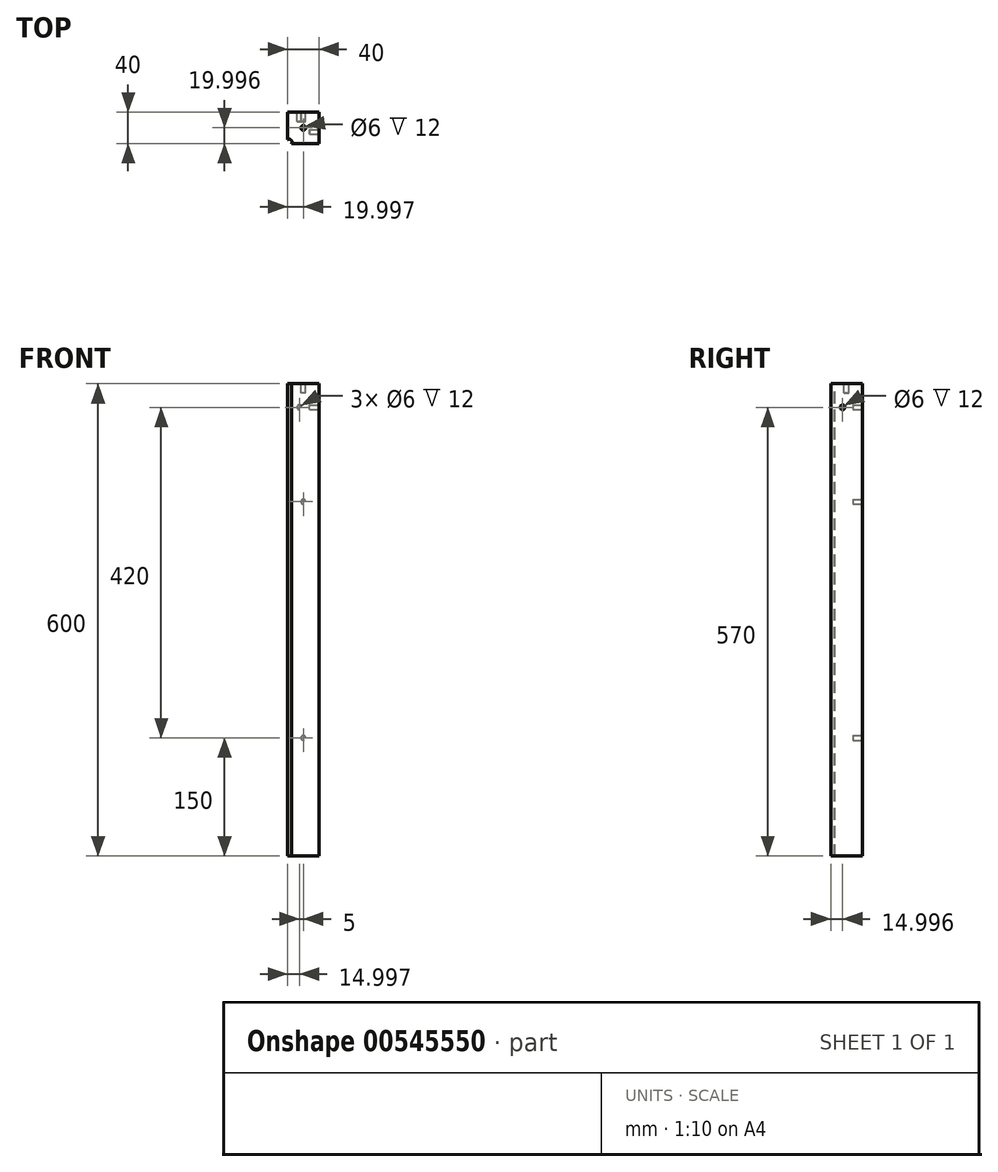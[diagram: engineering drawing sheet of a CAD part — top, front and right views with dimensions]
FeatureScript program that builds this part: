
annotation { "Feature Type Name" : "Feature", "Feature Type Description" : "" }
export const myFeature = defineFeature(function(context is Context, id is Id, definition is map)
    precondition{}
    {
        {
            var Q0;
            Q0=qCreatedBy(makeId("Top.planeOp"),FACE);
            var sketch = newSketch(context, id + "F0", { "sketchPlane" : qUnion([Q0])});
            skLineSegment(sketch, "E0.bottom", {"start": v(-52.47, 52.39) * mm, "end": v(-12.47, 52.39) * mm});
            skLineSegment(sketch, "E0.top", {"start": v(-52.47, 12.39) * mm, "end": v(-12.47, 12.39) * mm});
            skLineSegment(sketch, "E0.left", {"start": v(-52.47, 52.39) * mm, "end": v(-52.47, 12.39) * mm});
            skLineSegment(sketch, "E0.right", {"start": v(-12.47, 52.39) * mm, "end": v(-12.47, 12.39) * mm});
            skSolve(sketch);
        }
        {
            var Q0;
            Q0=makeQuery(id+"F0.imprint","IMPRINT",FACE,{"disambiguationData":[TD([[makeQuery(id+"F0.imprint","IMPRINT",EDGE,{"derivedFrom":sQuery(id+"F0.wireOp",EDGE,"E0.bottom")}),-1.0]])]});
            extrude(context, id + "F1", {"entities" : qUnion([Q0]), "depth" : 600 * mm, "offsetDistance" : 25 * mm});
        }
        {
            var Q0;
            Q0=makeQuery(id+"F1.opExtrude","SWEPT_FACE",FACE,{"disambiguationData":[OSD([sQuery(id+"F0.wireOp",EDGE,"E0.right")])]});
            var sketch = newSketch(context, id + "F2", { "sketchPlane" : qUnion([Q0])});
            skCircle(sketch, "E1", {"center": v(27.39, 570) * mm, "radius": 3 * mm});
            skSolve(sketch);
        }
        {
            var Q0;
            Q0=makeQuery(id+"F2.imprint","IMPRINT",FACE,{"disambiguationData":[TD([[makeQuery(id+"F2.imprint","IMPRINT",EDGE,{"derivedFrom":sQuery(id+"F2.wireOp",EDGE,"E1")}),1.0]])]});
            extrude(context, id + "F3", {"entities" : qUnion([Q0]), "operationType" : NewBodyOperationType.REMOVE, "oppositeDirection" : true, "depth" : 12 * mm, "offsetDistance" : 25 * mm});
        }
        {
            var Q0;
            Q0=makeQuery(id+"F1.opExtrude","SWEPT_FACE",FACE,{"disambiguationData":[OSD([sQuery(id+"F0.wireOp",EDGE,"E0.bottom")])]});
            var sketch = newSketch(context, id + "F4", { "sketchPlane" : qUnion([Q0])});
            skCircle(sketch, "E2", {"center": v(37.47, 570) * mm, "radius": 3 * mm});
            skCircle(sketch, "E3", {"center": v(32.47, 450) * mm, "radius": 3 * mm});
            skSolve(sketch);
        }
        {
            var Q0;
            Q0=makeQuery(id+"F4.imprint","IMPRINT",FACE,{"disambiguationData":[TD([[makeQuery(id+"F4.imprint","IMPRINT",EDGE,{"derivedFrom":sQuery(id+"F4.wireOp",EDGE,"E2")}),1.0]])]});
            extrude(context, id + "F5", {"entities" : qUnion([Q0]), "operationType" : NewBodyOperationType.REMOVE, "oppositeDirection" : true, "depth" : 12 * mm, "offsetDistance" : 25 * mm});
        }
        {
            var Q0;
            Q0=makeQuery(id+"F1.opExtrude","CAP_FACE",FACE,{"disambiguationData":[OSD([sQuery(id+"F0.wireOp",EDGE,"E0.bottom"),sQuery(id+"F0.wireOp",EDGE,"E0.top"),sQuery(id+"F0.wireOp",EDGE,"E0.left"),sQuery(id+"F0.wireOp",EDGE,"E0.right")])],"isStart":false});
            var sketch = newSketch(context, id + "F6", { "sketchPlane" : qUnion([Q0])});
            skCircle(sketch, "E4", {"center": v(-50.47, 14.39) * mm, "radius": 3.54 * mm});
            skSolve(sketch);
        }
        {
            var Q0;
            {var subQ0=sQuery(id+"F6.wireOp",EDGE,"E4");var subQ1=makeQuery(id+"F1.opExtrude","CAP_EDGE",EDGE,{"disambiguationData":[OSD([sQuery(id+"F0.wireOp",EDGE,"E0.top")])],"isStart":false});var subQ2=makeQuery(id+"F6.imprint","INTERSECT",VERTEX,{"derivedFrom":[subQ1,subQ0]});Q0=makeQuery(id+"F6.imprint","IMPRINT",FACE,{"disambiguationData":[TD([[makeQuery(id+"F6.imprint","IMPRINT",EDGE,{"disambiguationData":[TD([[subQ2,-1.0]])],"derivedFrom":subQ0}),1.0]])]});}
            extrude(context, id + "F7", {"entities" : qUnion([Q0]), "operationType" : NewBodyOperationType.REMOVE, "oppositeDirection" : true, "depth" : 600 * mm, "offsetDistance" : 25 * mm});
        }
        {
            var Q0;
            Q0=makeQuery(id+"F1.opExtrude","CAP_FACE",FACE,{"disambiguationData":[OSD([sQuery(id+"F0.wireOp",EDGE,"E0.bottom"),sQuery(id+"F0.wireOp",EDGE,"E0.top"),sQuery(id+"F0.wireOp",EDGE,"E0.left"),sQuery(id+"F0.wireOp",EDGE,"E0.right")])],"isStart":false});
            var sketch = newSketch(context, id + "F8", { "sketchPlane" : qUnion([Q0])});
            skPoint(sketch, "E5.centerSnap0", {"position": v(-52.47, 34.85) * mm});
            skPoint(sketch, "E5.centerSnap1", {"position": v(-32.47, 52.39) * mm});
            skCircle(sketch, "E6", {"center": v(-32.47, 32.39) * mm, "radius": 3 * mm});
            skSolve(sketch);
        }
        {
            var Q0;
            Q0=makeQuery(id+"F8.imprint","IMPRINT",FACE,{"disambiguationData":[TD([[makeQuery(id+"F8.imprint","IMPRINT",EDGE,{"derivedFrom":sQuery(id+"F8.wireOp",EDGE,"E6")}),1.0]])]});
            extrude(context, id + "F9", {"entities" : qUnion([Q0]), "operationType" : NewBodyOperationType.REMOVE, "oppositeDirection" : true, "depth" : 12 * mm, "offsetDistance" : 25 * mm});
        }
        {
            var Q0;
            Q0=makeQuery(id+"F4.imprint","IMPRINT",FACE,{"disambiguationData":[TD([[makeQuery(id+"F4.imprint","IMPRINT",EDGE,{"derivedFrom":sQuery(id+"F4.wireOp",EDGE,"E3")}),1.0]])]});
            var Q1;
            Q1=sQuery(id+"F4.wireOp",EDGE,"E3");
            extrude(context, id + "F10", {"entities" : qUnion([Q0]), "operationType" : NewBodyOperationType.REMOVE, "surfaceEntities" : qUnion([Q1]), "oppositeDirection" : true, "depth" : 12 * mm, "offsetDistance" : 25 * mm});
        }
        {
            var Q0;
            Q0=makeQuery(id+"F4.imprint","IMPRINT",FACE,{"disambiguationData":[TD([[makeQuery(id+"F4.imprint","IMPRINT",EDGE,{"derivedFrom":sQuery(id+"F4.wireOp",EDGE,"E2")}),-1.0]])]});
            var sketch = newSketch(context, id + "F11", { "sketchPlane" : qUnion([Q0])});
            skCircle(sketch, "E7", {"center": v(32.47, 150) * mm, "radius": 3 * mm});
            skSolve(sketch);
        }
        {
            var Q0;
            Q0=makeQuery(id+"F11.imprint","IMPRINT",FACE,{"disambiguationData":[TD([[makeQuery(id+"F11.imprint","IMPRINT",EDGE,{"derivedFrom":sQuery(id+"F11.wireOp",EDGE,"E7")}),1.0]])]});
            extrude(context, id + "F12", {"entities" : qUnion([Q0]), "operationType" : NewBodyOperationType.REMOVE, "oppositeDirection" : true, "depth" : 12 * mm, "offsetDistance" : 25 * mm});
        }
    });
